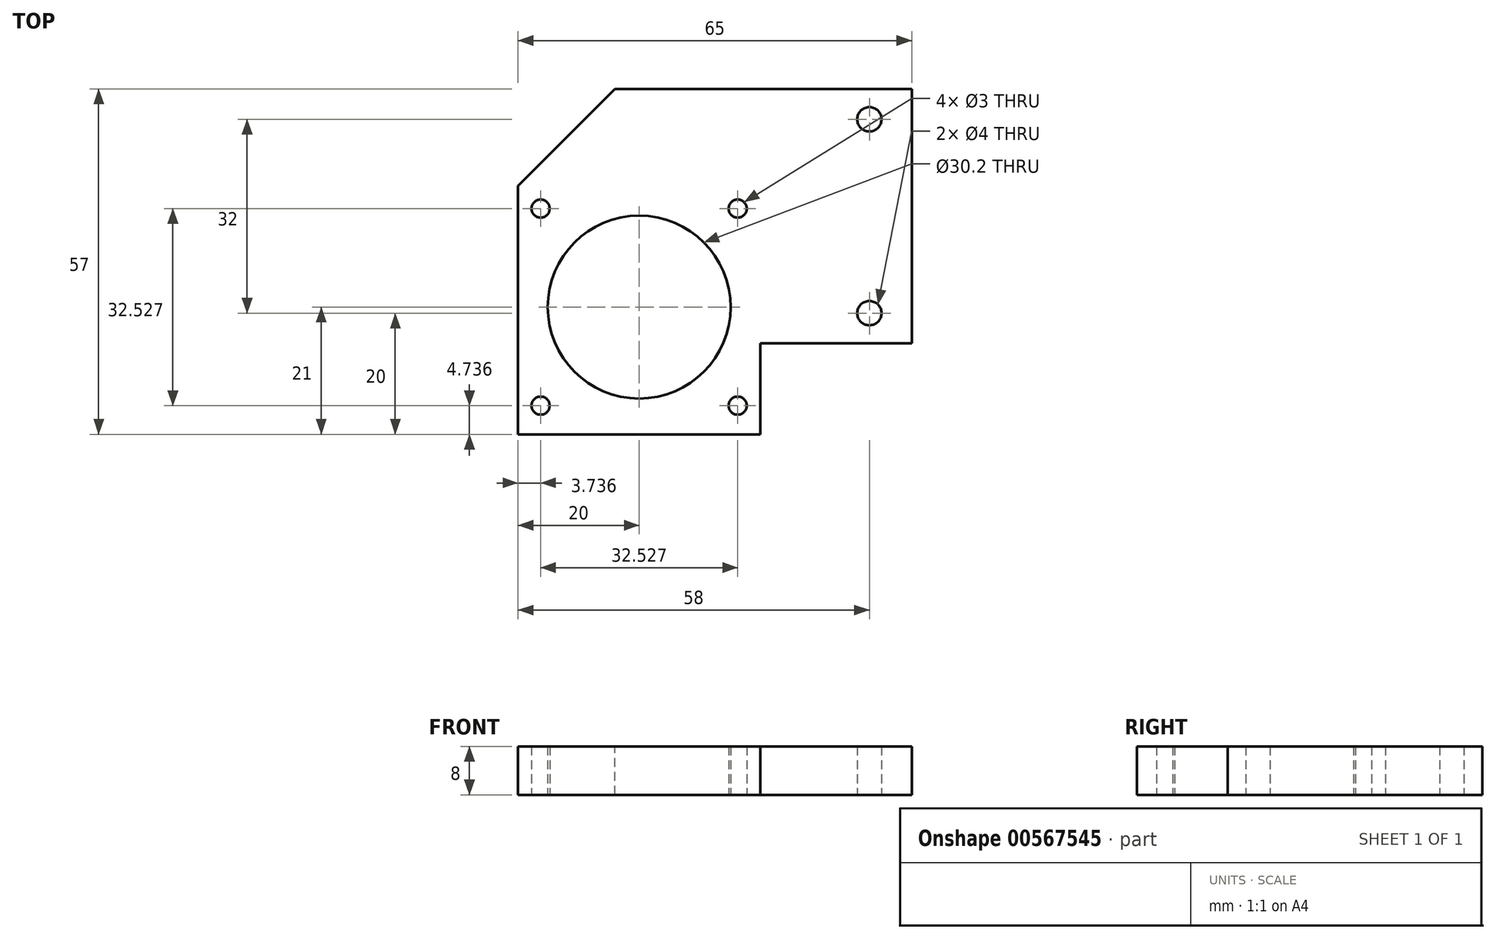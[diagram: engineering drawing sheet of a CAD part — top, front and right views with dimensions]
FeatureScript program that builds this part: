
annotation { "Feature Type Name" : "Feature", "Feature Type Description" : "" }
export const myFeature = defineFeature(function(context is Context, id is Id, definition is map)
    precondition{}
    {
        {
            var Q0;
            Q0=qCreatedBy(makeId("Top.planeOp"),FACE);
            var sketch = newSketch(context, id + "F0", { "sketchPlane" : qUnion([Q0])});
            skLineSegment(sketch, "E0.top", {"start": v(32.5, 21) * mm, "end": v(-32.5, 21) * mm});
            skLineSegment(sketch, "E0.left", {"start": v(32.5, -21) * mm, "end": v(32.5, 21) * mm});
            skLineSegment(sketch, "E0.right", {"start": v(-32.5, -21) * mm, "end": v(-32.5, 21) * mm});
            skPoint(sketch, "E0.middle", {"position": v(0, 0) * mm});
            skCircle(sketch, "E1", {"center": v(25.5, -16) * mm, "radius": 2 * mm});
            skCircle(sketch, "E2", {"center": v(25.5, 16) * mm, "radius": 2 * mm});
            skCircle(sketch, "E3", {"center": v(-12.5, -15) * mm, "radius": 15.1 * mm});
            skCircle(sketch, "E4", {"center": v(-12.5, -15) * mm, "radius": 23 * mm, "construction": true});
            skLineSegment(sketch, "E5.bottom", {"start": v(-28.76, 1.26) * mm, "end": v(3.76, 1.26) * mm, "construction": true});
            skLineSegment(sketch, "E5.top", {"start": v(-28.76, -31.26) * mm, "end": v(3.76, -31.26) * mm, "construction": true});
            skLineSegment(sketch, "E5.left", {"start": v(-28.76, 1.26) * mm, "end": v(-28.76, -31.26) * mm, "construction": true});
            skLineSegment(sketch, "E5.right", {"start": v(3.76, 1.26) * mm, "end": v(3.76, -31.26) * mm, "construction": true});
            skCircle(sketch, "E6", {"center": v(3.76, 1.26) * mm, "radius": 1.5 * mm});
            skCircle(sketch, "E7", {"center": v(-28.76, 1.26) * mm, "radius": 1.5 * mm});
            skCircle(sketch, "E8", {"center": v(-28.76, -31.26) * mm, "radius": 1.5 * mm});
            skCircle(sketch, "E9", {"center": v(3.76, -31.26) * mm, "radius": 1.5 * mm});
            skLineSegment(sketch, "E10", {"start": v(-32.5, -21) * mm, "end": v(-32.5, -36) * mm});
            skLineSegment(sketch, "E11", {"start": v(-32.5, -36) * mm, "end": v(7.5, -36) * mm});
            skLineSegment(sketch, "E12", {"start": v(7.5, -36) * mm, "end": v(7.5, -21) * mm});
            skLineSegment(sketch, "E13", {"start": v(7.5, -21) * mm, "end": v(32.5, -21) * mm});
            skSolve(sketch);
        }
        {
            var Q0;
            Q0 = qSketchRegion(id + "F0", true);
            extrude(context, id + "F1", {"entities" : qUnion([Q0]), "depth" : 8 * mm, "offsetDistance" : 25 * mm});
        }
        {
            var Q0;
            Q0=makeQuery(id+"F1.opExtrude","SWEPT_EDGE",EDGE,{"disambiguationData":[OSD([sQuery(id+"F0.wireOp",EDGE,"E0.top"),sQuery(id+"F0.wireOp",EDGE,"E0.right")])]});
            chamfer(context, id + "F2", {"entities" : qUnion([Q0]), "width" : 16 * mm, "tangentPropagation" : true});
        }
    });
